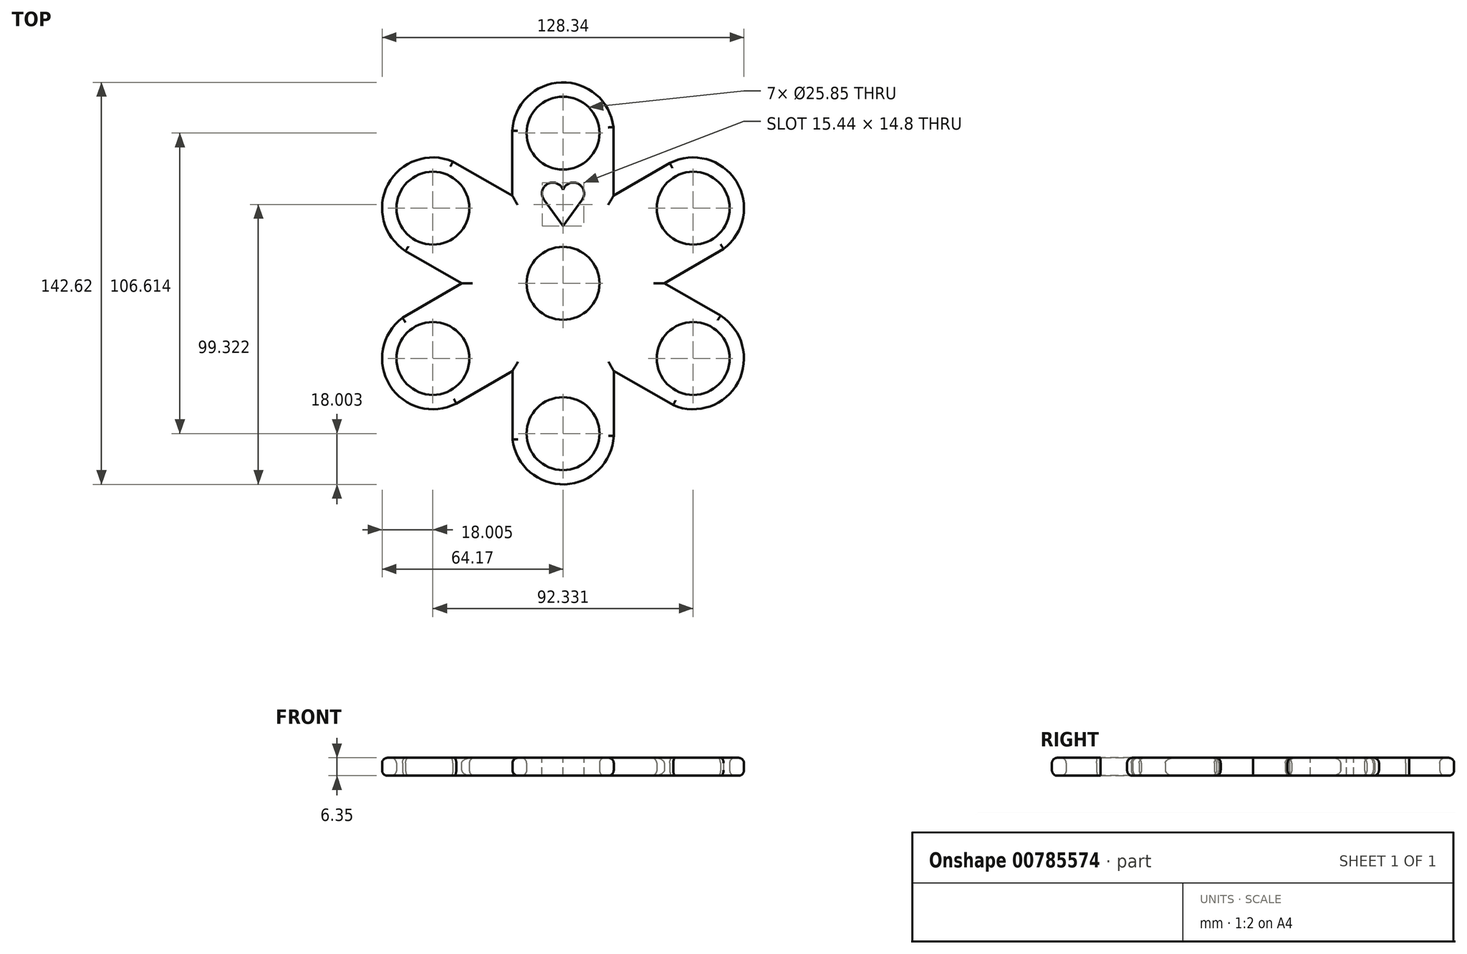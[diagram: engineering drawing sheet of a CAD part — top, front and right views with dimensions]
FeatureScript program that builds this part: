
annotation { "Feature Type Name" : "Feature", "Feature Type Description" : "" }
export const myFeature = defineFeature(function(context is Context, id is Id, definition is map)
    precondition{}
    {
        {
            var Q0;
            Q0=qCreatedBy(makeId("Top.planeOp"),FACE);
            var sketch = newSketch(context, id + "F0", { "sketchPlane" : qUnion([Q0])});
            skCircle(sketch, "E0", {"center": v(0, 0) * mm, "radius": 12.93 * mm});
            skArc(sketch, "E1", {"start": v(-17.99, 0.79) * mm, "mid": v(-0.35, -18) * mm, "end": v(18, 0.08) * mm});
            skCircle(sketch, "E2", {"center": v(0, 53.3) * mm, "radius": 12.93 * mm});
            skArc(sketch, "E3", {"start": v(17.9, 51.27) * mm, "mid": v(0.63, 71.3) * mm, "end": v(-17.99, 52.52) * mm});
            skLineSegment(sketch, "E4", {"start": v(-17.99, 54.1) * mm, "end": v(-17.99, 0) * mm});
            skLineSegment(sketch, "E5", {"start": v(18, 0) * mm, "end": v(17.88, 55.43) * mm});
            skSolve(sketch);
        }
        {
            var Q0;
            Q0=makeQuery(id+"F0.imprint","IMPRINT",FACE,{"disambiguationData":[TD([[makeQuery(id+"F0.imprint","IMPRINT",EDGE,{"derivedFrom":sQuery(id+"F0.wireOp",EDGE,"E0")}),-1.0]])]});
            extrude(context, id + "F1", {"entities" : qUnion([Q0]), "depth" : 6.35 * mm, "offsetDistance" : 25.4 * mm});
        }
        {
            var Q0;
            Q0=makeQuery(id+"F1.opExtrude","SWEPT_BODY",BODY,{"disambiguationData":[OSD([sQuery(id+"F0.wireOp",EDGE,"E0"),sQuery(id+"F0.wireOp",EDGE,"E1"),sQuery(id+"F0.wireOp",EDGE,"E2"),sQuery(id+"F0.wireOp",EDGE,"E3"),sQuery(id+"F0.wireOp",EDGE,"E4"),sQuery(id+"F0.wireOp",EDGE,"E5")])]});
            var Q1;
            Q1=makeQuery(id+"F1.opExtrude","CAP_EDGE",EDGE,{"disambiguationData":[OSD([sQuery(id+"F0.wireOp",EDGE,"E0")])],"isStart":false});
            circularPattern(context, id + "F2", {"entities" : qUnion([Q0]), "axis" : qUnion([Q1]), "angle" : 360 * degree, "instanceCount" : 6, "equalSpace" : true});
        }
        {
            var Q0;
            Q0=makeQuery(id+"F1.opExtrude","SWEPT_BODY",BODY,{"disambiguationData":[OSD([sQuery(id+"F0.wireOp",EDGE,"E0"),sQuery(id+"F0.wireOp",EDGE,"E1"),sQuery(id+"F0.wireOp",EDGE,"E2"),sQuery(id+"F0.wireOp",EDGE,"E3"),sQuery(id+"F0.wireOp",EDGE,"E4"),sQuery(id+"F0.wireOp",EDGE,"E5")])]});
            var Q1;
            Q1=makeQuery(id+"F2.opPattern","COPY",BODY,{"derivedFrom":makeQuery(id+"F1.opExtrude","SWEPT_BODY",BODY,{"disambiguationData":[OSD([sQuery(id+"F0.wireOp",EDGE,"E0"),sQuery(id+"F0.wireOp",EDGE,"E1"),sQuery(id+"F0.wireOp",EDGE,"E2"),sQuery(id+"F0.wireOp",EDGE,"E3"),sQuery(id+"F0.wireOp",EDGE,"E4"),sQuery(id+"F0.wireOp",EDGE,"E5")])]}),"instanceName":"2"});
            var Q2;
            Q2=makeQuery(id+"F2.opPattern","COPY",BODY,{"derivedFrom":makeQuery(id+"F1.opExtrude","SWEPT_BODY",BODY,{"disambiguationData":[OSD([sQuery(id+"F0.wireOp",EDGE,"E0"),sQuery(id+"F0.wireOp",EDGE,"E1"),sQuery(id+"F0.wireOp",EDGE,"E2"),sQuery(id+"F0.wireOp",EDGE,"E3"),sQuery(id+"F0.wireOp",EDGE,"E4"),sQuery(id+"F0.wireOp",EDGE,"E5")])]}),"instanceName":"1"});
            var Q3;
            Q3=makeQuery(id+"F2.opPattern","COPY",BODY,{"derivedFrom":makeQuery(id+"F1.opExtrude","SWEPT_BODY",BODY,{"disambiguationData":[OSD([sQuery(id+"F0.wireOp",EDGE,"E0"),sQuery(id+"F0.wireOp",EDGE,"E1"),sQuery(id+"F0.wireOp",EDGE,"E2"),sQuery(id+"F0.wireOp",EDGE,"E3"),sQuery(id+"F0.wireOp",EDGE,"E4"),sQuery(id+"F0.wireOp",EDGE,"E5")])]}),"instanceName":"3"});
            var Q4;
            Q4=makeQuery(id+"F2.opPattern","COPY",BODY,{"derivedFrom":makeQuery(id+"F1.opExtrude","SWEPT_BODY",BODY,{"disambiguationData":[OSD([sQuery(id+"F0.wireOp",EDGE,"E0"),sQuery(id+"F0.wireOp",EDGE,"E1"),sQuery(id+"F0.wireOp",EDGE,"E2"),sQuery(id+"F0.wireOp",EDGE,"E3"),sQuery(id+"F0.wireOp",EDGE,"E4"),sQuery(id+"F0.wireOp",EDGE,"E5")])]}),"instanceName":"4"});
            var Q5;
            Q5=makeQuery(id+"F2.opPattern","COPY",BODY,{"derivedFrom":makeQuery(id+"F1.opExtrude","SWEPT_BODY",BODY,{"disambiguationData":[OSD([sQuery(id+"F0.wireOp",EDGE,"E0"),sQuery(id+"F0.wireOp",EDGE,"E1"),sQuery(id+"F0.wireOp",EDGE,"E2"),sQuery(id+"F0.wireOp",EDGE,"E3"),sQuery(id+"F0.wireOp",EDGE,"E4"),sQuery(id+"F0.wireOp",EDGE,"E5")])]}),"instanceName":"5"});
            booleanBodies(context, id + "F3", {"operationType" : BooleanOperationType.UNION, "tools" : qUnion([Q0, Q1, Q2, Q3, Q4, Q5])});
        }
        {
            var Q0;
            {var subQ0=makeQuery(id+"F1.opExtrude","CAP_FACE",FACE,{"disambiguationData":[OSD([sQuery(id+"F0.wireOp",EDGE,"E0"),sQuery(id+"F0.wireOp",EDGE,"E1"),sQuery(id+"F0.wireOp",EDGE,"E2"),sQuery(id+"F0.wireOp",EDGE,"E3"),sQuery(id+"F0.wireOp",EDGE,"E4"),sQuery(id+"F0.wireOp",EDGE,"E5")])],"isStart":false});Q0=makeQuery(id+"F3.opBoolean","MERGE",FACE,{"derivedFrom":[subQ0,makeQuery(id+"F2.opPattern","COPY",FACE,{"derivedFrom":subQ0,"instanceName":"1"}),makeQuery(id+"F2.opPattern","COPY",FACE,{"derivedFrom":subQ0,"instanceName":"2"}),makeQuery(id+"F2.opPattern","COPY",FACE,{"derivedFrom":subQ0,"instanceName":"3"}),makeQuery(id+"F2.opPattern","COPY",FACE,{"derivedFrom":subQ0,"instanceName":"4"}),makeQuery(id+"F2.opPattern","COPY",FACE,{"derivedFrom":subQ0,"instanceName":"5"})]});}
            var Q1;
            {var subQ0=makeQuery(id+"F1.opExtrude","CAP_FACE",FACE,{"disambiguationData":[OSD([sQuery(id+"F0.wireOp",EDGE,"E0"),sQuery(id+"F0.wireOp",EDGE,"E1"),sQuery(id+"F0.wireOp",EDGE,"E2"),sQuery(id+"F0.wireOp",EDGE,"E3"),sQuery(id+"F0.wireOp",EDGE,"E4"),sQuery(id+"F0.wireOp",EDGE,"E5")])],"isStart":true});Q1=makeQuery(id+"F3.opBoolean","MERGE",FACE,{"derivedFrom":[subQ0,makeQuery(id+"F2.opPattern","COPY",FACE,{"derivedFrom":subQ0,"instanceName":"1"}),makeQuery(id+"F2.opPattern","COPY",FACE,{"derivedFrom":subQ0,"instanceName":"2"}),makeQuery(id+"F2.opPattern","COPY",FACE,{"derivedFrom":subQ0,"instanceName":"3"}),makeQuery(id+"F2.opPattern","COPY",FACE,{"derivedFrom":subQ0,"instanceName":"4"}),makeQuery(id+"F2.opPattern","COPY",FACE,{"derivedFrom":subQ0,"instanceName":"5"})]});}
            fillet(context, id + "F4", {"entities" : qUnion([Q0, Q1]), "radius" : 1.9 * mm, "tangentPropagation" : true, "allowEdgeOverflow" : false});
        }
        {
            var Q0;
            {var subQ0=makeQuery(id+"F1.opExtrude","CAP_FACE",FACE,{"disambiguationData":[OSD([sQuery(id+"F0.wireOp",EDGE,"E0"),sQuery(id+"F0.wireOp",EDGE,"E1"),sQuery(id+"F0.wireOp",EDGE,"E2"),sQuery(id+"F0.wireOp",EDGE,"E3"),sQuery(id+"F0.wireOp",EDGE,"E4"),sQuery(id+"F0.wireOp",EDGE,"E5")])],"isStart":false});Q0=makeQuery(id+"F3.opBoolean","MERGE",FACE,{"derivedFrom":[subQ0,makeQuery(id+"F2.opPattern","COPY",FACE,{"derivedFrom":subQ0,"instanceName":"1"}),makeQuery(id+"F2.opPattern","COPY",FACE,{"derivedFrom":subQ0,"instanceName":"2"}),makeQuery(id+"F2.opPattern","COPY",FACE,{"derivedFrom":subQ0,"instanceName":"3"}),makeQuery(id+"F2.opPattern","COPY",FACE,{"derivedFrom":subQ0,"instanceName":"4"}),makeQuery(id+"F2.opPattern","COPY",FACE,{"derivedFrom":subQ0,"instanceName":"5"})]});}
            var sketch = newSketch(context, id + "F5", { "sketchPlane" : qUnion([Q0])});
            skLineSegment(sketch, "E6", {"start": v(0, 20.3) * mm, "end": v(6.74, 29.63) * mm});
            skArc(sketch, "E7", {"start": v(6.74, 29.63) * mm, "mid": v(5.42, 35.3) * mm, "end": v(0, 33.2) * mm});
            skArc(sketch, "E8.MirrorCS", {"start": v(-6.74, 29.63) * mm, "mid": v(-5.42, 35.3) * mm, "end": v(0, 33.2) * mm});
            skLineSegment(sketch, "E9.MirrorCS", {"start": v(0, 20.3) * mm, "end": v(-6.74, 29.63) * mm});
            skSolve(sketch);
        }
        {
            var Q0;
            Q0=makeQuery(id+"F5.imprint","IMPRINT",FACE,{"disambiguationData":[TD([[makeQuery(id+"F5.imprint","IMPRINT",EDGE,{"derivedFrom":sQuery(id+"F5.wireOp",EDGE,"E6")}),1.0]])]});
            extrude(context, id + "F6", {"entities" : qUnion([Q0]), "operationType" : NewBodyOperationType.REMOVE, "oppositeDirection" : true, "depth" : 25.4 * mm, "offsetDistance" : 25.4 * mm});
        }
    });
